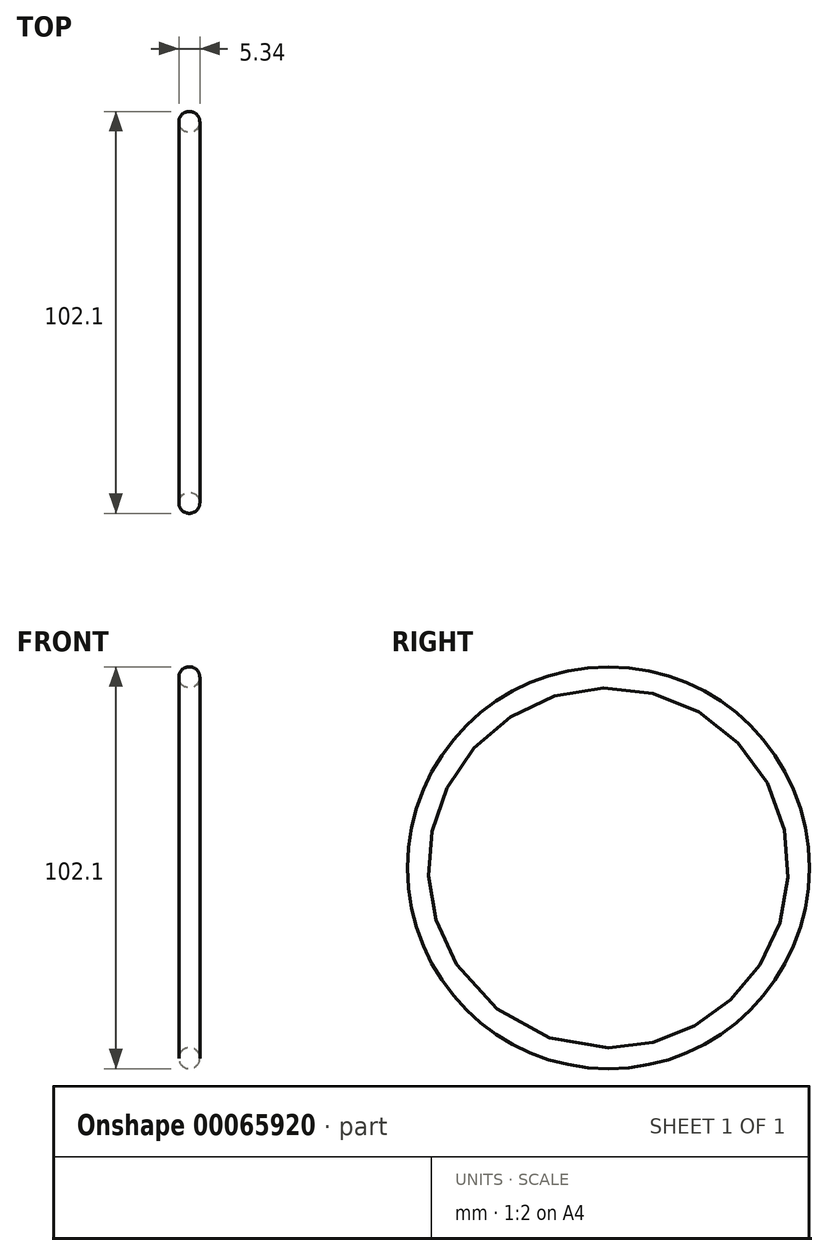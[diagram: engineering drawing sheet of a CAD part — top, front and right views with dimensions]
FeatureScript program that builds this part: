
annotation { "Feature Type Name" : "Feature", "Feature Type Description" : "" }
export const myFeature = defineFeature(function(context is Context, id is Id, definition is map)
    precondition{}
    {
        {
            var Q0;
            Q0=qCreatedBy(makeId("Front.planeOp"),FACE);
            var sketch = newSketch(context, id + "F0", { "sketchPlane" : qUnion([Q0])});
            skLineSegment(sketch, "E0", {"start": v(0, 0) * mm, "end": v(-6.06, 0) * mm, "construction": true});
            skCircle(sketch, "E1", {"center": v(0, 48.39) * mm, "radius": 2.67 * mm});
            skSolve(sketch);
        }
        {
            var Q0;
            Q0=makeQuery(id+"F0.imprint","IMPRINT",FACE,{"disambiguationData":[TD([[makeQuery(id+"F0.imprint","IMPRINT",EDGE,{"derivedFrom":sQuery(id+"F0.wireOp",EDGE,"E1")}),1.0]])]});
            var Q1;
            Q1=sQuery(id+"F0.wireOp",EDGE,"E0");
            revolve(context, id + "F1", {"entities" : qUnion([Q0]), "axis" : qUnion([Q1]), "revolveType" : RevolveType.FULL});
        }
    });
